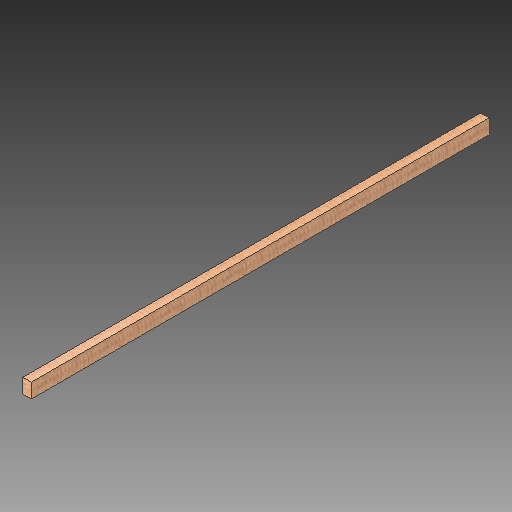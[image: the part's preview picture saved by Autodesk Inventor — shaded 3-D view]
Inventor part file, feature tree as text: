
AUTODESK INVENTOR PART (.ipt)
format: ipt  version: 2018 (Build 220112000, 112)  size: 108,032 bytes
history: native  units: mm
features: extrude x1, sketch x1
ambient origin geometry x8: Origin, YZ Plane, XZ Plane, XY Plane, X Axis, Y Axis, Z Axis, Center Point
bodies: Solid1 (feature_tree)
feature tree (2):
  extrude  "Extrusion1"  Depth=60.0mm
  sketch  "Sketch1"  dims[d0=35.0mm d1=60.0mm d2=1884.0mm d3=0.0mm]
